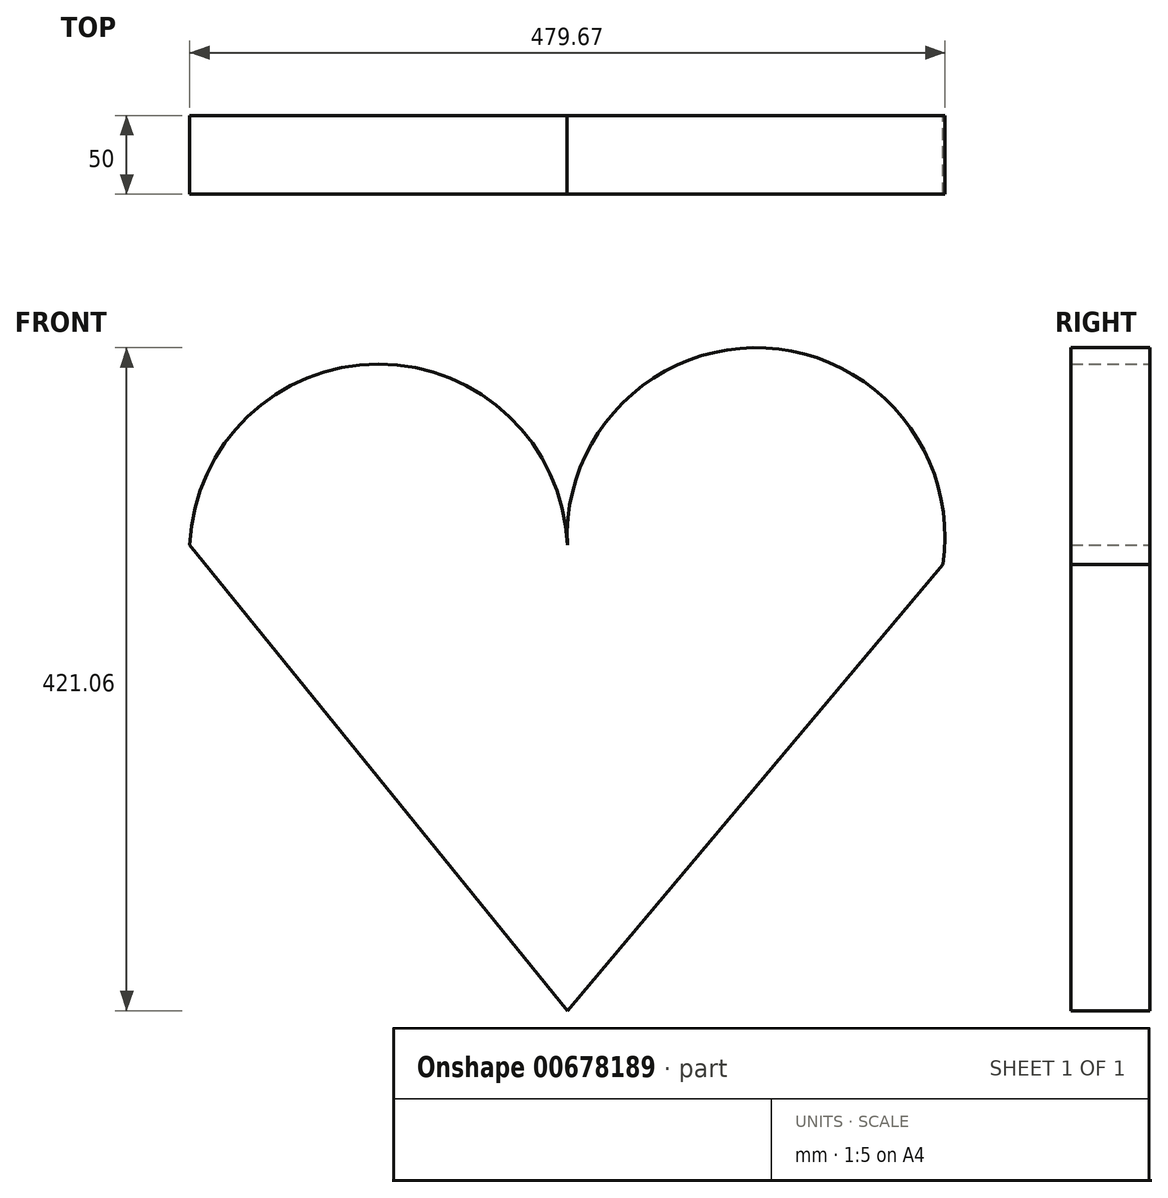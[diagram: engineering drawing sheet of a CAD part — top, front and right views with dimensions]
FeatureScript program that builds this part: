
annotation { "Feature Type Name" : "Feature", "Feature Type Description" : "" }
export const myFeature = defineFeature(function(context is Context, id is Id, definition is map)
    precondition{}
    {
        {
            var Q0;
            Q0=qCreatedBy(makeId("Front.planeOp"),FACE);
            var sketch = newSketch(context, id + "F0", { "sketchPlane" : qUnion([Q0])});
            skCircle(sketch, "E0", {"center": v(0, 0) * mm, "radius": 53.72 * mm});
            skCircle(sketch, "E1", {"center": v(0, 0) * mm, "radius": 58.65 * mm, "construction": true});
            skCircle(sketch, "E2", {"center": v(0, 0) * mm, "radius": 63.5 * mm, "construction": true});
            skLineSegment(sketch, "E3", {"start": v(0, 0) * mm, "end": v(0, 78.84) * mm, "construction": true});
            skLineSegment(sketch, "E4", {"start": v(0, 0) * mm, "end": v(-5.91, 90.2) * mm, "construction": true});
            skPoint(sketch, "E5.startSnap0", {"position": v(0, 39.42) * mm});
            skLineSegment(sketch, "E6", {"start": v(0, 58.65) * mm, "end": v(-64.13, 58.65) * mm, "construction": true});
            skLineSegment(sketch, "E7", {"start": v(0, 58.65) * mm, "end": v(-66.32, 34.51) * mm, "construction": true});
            skCircle(sketch, "E8", {"center": v(0, 0) * mm, "radius": 55.11 * mm, "construction": true});
            skCircle(sketch, "E9", {"center": v(0, 58.65) * mm, "radius": 14.6 * mm, "construction": true});
            skCircle(sketch, "E10", {"center": v(-13.72, 53.65) * mm, "radius": 14.6 * mm, "construction": true});
            skArc(sketch, "E11", {"start": v(0.88, 53.71) * mm, "mid": v(0.64, 56.22) * mm, "end": v(0, 58.65) * mm});
            skArc(sketch, "E12", {"start": v(0, 58.65) * mm, "mid": v(-1.1, 61.03) * mm, "end": v(-2.63, 63.15) * mm});
            skArc(sketch, "E13.MirrorCS", {"start": v(-7.66, 58.15) * mm, "mid": v(-6.88, 60.65) * mm, "end": v(-5.64, 62.95) * mm});
            skCircle(sketch, "E14.MirrorC", {"center": v(6.6, 54.99) * mm, "radius": 14.6 * mm, "construction": true});
            skArc(sketch, "E15.MirrorCS", {"start": v(-7.88, 53.14) * mm, "mid": v(-7.97, 55.65) * mm, "end": v(-7.66, 58.15) * mm});
            skArc(sketch, "E16", {"start": v(-2.63, 63.15) * mm, "mid": v(-4.14, 63.24) * mm, "end": v(-5.64, 62.95) * mm});
            skCircle(sketch, "E17", {"center": v(0, 0) * mm, "radius": 37.5 * mm});
            skLineSegment(sketch, "E18", {"start": v(-18.41, 23.71) * mm, "end": v(-5.46, 4.6) * mm});
            skLineSegment(sketch, "E19", {"start": v(-5.46, 4.6) * mm, "end": v(1.07, 20.93) * mm});
            skLineSegment(sketch, "E20", {"start": v(1.07, 20.93) * mm, "end": v(16.07, -7.38) * mm});
            skLineSegment(sketch, "E21", {"start": v(16.07, -7.38) * mm, "end": v(-13.09, -2.9) * mm});
            skLineSegment(sketch, "E22", {"start": v(-13.09, -2.9) * mm, "end": v(-18.41, 23.71) * mm});
            skSolve(sketch);
        }
        {
            var Q0;
            {var subQ0=sQuery(id+"F0.wireOp",EDGE,"E0");var subQ1=makeQuery(id+"F0.imprint","INTERSECT",VERTEX,{"derivedFrom":[subQ0,sQuery(id+"F0.wireOp",EDGE,"E11")]});Q0=makeQuery(id+"F0.imprint","IMPRINT",FACE,{"disambiguationData":[TD([[makeQuery(id+"F0.imprint","IMPRINT",EDGE,{"disambiguationData":[TD([[subQ1,-1.0]])],"derivedFrom":subQ0}),1.0]])]});}
            var Q1;
            {var subQ0=sQuery(id+"F0.wireOp",EDGE,"E11");Q1=makeQuery(id+"F0.imprint","IMPRINT",FACE,{"disambiguationData":[TD([[makeQuery(id+"F0.imprint","IMPRINT",EDGE,{"derivedFrom":subQ0}),1.0]])]});}
            extrude(context, id + "F1", {"entities" : qUnion([Q0, Q1]), "depth" : 25 * mm, "offsetDistance" : 25 * mm});
        }
        {
            var Q0;
            Q0=makeQuery(id+"F1.opExtrude","SWEPT_BODY",BODY,{"disambiguationData":[OSD([sQuery(id+"F0.wireOp",EDGE,"E0"),sQuery(id+"F0.wireOp",EDGE,"E11"),sQuery(id+"F0.wireOp",EDGE,"E12"),sQuery(id+"F0.wireOp",EDGE,"E13.MirrorCS"),sQuery(id+"F0.wireOp",EDGE,"E15.MirrorCS"),sQuery(id+"F0.wireOp",EDGE,"E16")])]});
            var Q1;
            Q1=makeQuery(id+"F1.opExtrude","SWEPT_FACE",FACE,{"disambiguationData":[OSD([sQuery(id+"F0.wireOp",EDGE,"E0")])]});
            circularPattern(context, id + "F2", {"entities" : qUnion([Q0]), "axis" : qUnion([Q1]), "angle" : 360 * degree, "instanceCount" : 24, "equalSpace" : true});
        }
        {
            var Q0;
            Q0=makeQuery(id+"F0.imprint","IMPRINT",FACE,{"disambiguationData":[TD([[makeQuery(id+"F0.imprint","IMPRINT",EDGE,{"derivedFrom":sQuery(id+"F0.wireOp",EDGE,"E17")}),1.0]])]});
            extrude(context, id + "F3", {"entities" : qUnion([Q0]), "operationType" : NewBodyOperationType.ADD, "depth" : 35 * mm, "offsetDistance" : 25 * mm});
        }
        {
            var Q0;
            {var subQ0=sQuery(id+"F0.wireOp",EDGE,"E17");var subQ1=makeQuery(id+"F1.opExtrude","CAP_FACE",FACE,{"disambiguationData":[OSD([sQuery(id+"F0.wireOp",EDGE,"E0"),sQuery(id+"F0.wireOp",EDGE,"E11"),sQuery(id+"F0.wireOp",EDGE,"E12"),sQuery(id+"F0.wireOp",EDGE,"E13.MirrorCS"),sQuery(id+"F0.wireOp",EDGE,"E15.MirrorCS"),sQuery(id+"F0.wireOp",EDGE,"E16"),subQ0])],"isStart":true});Q0=makeQuery(id+"F3.boolean.opBoolean","MERGE",FACE,{"derivedFrom":[subQ1,makeQuery(id+"F2.opPattern","COPY",FACE,{"derivedFrom":subQ1,"instanceName":"1"}),makeQuery(id+"F2.opPattern","COPY",FACE,{"derivedFrom":subQ1,"instanceName":"2"}),makeQuery(id+"F2.opPattern","COPY",FACE,{"derivedFrom":subQ1,"instanceName":"3"}),makeQuery(id+"F2.opPattern","COPY",FACE,{"derivedFrom":subQ1,"instanceName":"4"}),makeQuery(id+"F2.opPattern","COPY",FACE,{"derivedFrom":subQ1,"instanceName":"5"}),makeQuery(id+"F2.opPattern","COPY",FACE,{"derivedFrom":subQ1,"instanceName":"6"}),makeQuery(id+"F2.opPattern","COPY",FACE,{"derivedFrom":subQ1,"instanceName":"7"}),makeQuery(id+"F2.opPattern","COPY",FACE,{"derivedFrom":subQ1,"instanceName":"8"}),makeQuery(id+"F2.opPattern","COPY",FACE,{"derivedFrom":subQ1,"instanceName":"9"}),makeQuery(id+"F2.opPattern","COPY",FACE,{"derivedFrom":subQ1,"instanceName":"10"}),makeQuery(id+"F2.opPattern","COPY",FACE,{"derivedFrom":subQ1,"instanceName":"11"}),makeQuery(id+"F2.opPattern","COPY",FACE,{"derivedFrom":subQ1,"instanceName":"12"}),makeQuery(id+"F2.opPattern","COPY",FACE,{"derivedFrom":subQ1,"instanceName":"13"}),makeQuery(id+"F2.opPattern","COPY",FACE,{"derivedFrom":subQ1,"instanceName":"14"}),makeQuery(id+"F2.opPattern","COPY",FACE,{"derivedFrom":subQ1,"instanceName":"15"}),makeQuery(id+"F2.opPattern","COPY",FACE,{"derivedFrom":subQ1,"instanceName":"16"}),makeQuery(id+"F2.opPattern","COPY",FACE,{"derivedFrom":subQ1,"instanceName":"17"}),makeQuery(id+"F2.opPattern","COPY",FACE,{"derivedFrom":subQ1,"instanceName":"18"}),makeQuery(id+"F2.opPattern","COPY",FACE,{"derivedFrom":subQ1,"instanceName":"19"}),makeQuery(id+"F2.opPattern","COPY",FACE,{"derivedFrom":subQ1,"instanceName":"20"}),makeQuery(id+"F2.opPattern","COPY",FACE,{"derivedFrom":subQ1,"instanceName":"21"}),makeQuery(id+"F2.opPattern","COPY",FACE,{"derivedFrom":subQ1,"instanceName":"22"}),makeQuery(id+"F2.opPattern","COPY",FACE,{"derivedFrom":subQ1,"instanceName":"23"}),makeQuery(id+"F3.opExtrude","CAP_FACE",FACE,{"disambiguationData":[OSD([subQ0,sQuery(id+"F0.wireOp",EDGE,"E18"),sQuery(id+"F0.wireOp",EDGE,"E19"),sQuery(id+"F0.wireOp",EDGE,"E20"),sQuery(id+"F0.wireOp",EDGE,"E21"),sQuery(id+"F0.wireOp",EDGE,"E22")])],"isStart":true})]});}
            chamfer(context, id + "F4", {"entities" : qUnion([Q0]), "width" : 1 * mm, "tangentPropagation" : true});
        }
        {
            var Q0;
            Q0=qCreatedBy(makeId("Front.planeOp"),FACE);
            var sketch = newSketch(context, id + "F5", { "sketchPlane" : qUnion([Q0])});
            skArc(sketch, "E23", {"start": v(238.57, 66.06) * mm, "mid": v(126.17, 203.6) * mm, "end": v(0, 78.56) * mm});
            skArc(sketch, "E24", {"start": v(0, 78.56) * mm, "mid": v(-119.89, 193.4) * mm, "end": v(-239.78, 78.56) * mm});
            skLineSegment(sketch, "E25", {"start": v(0, -217.3) * mm, "end": v(-239.78, 78.56) * mm});
            skLineSegment(sketch, "E26", {"start": v(0, -217.3) * mm, "end": v(238.57, 66.06) * mm});
            skSolve(sketch);
        }
        {
            var Q0;
            {var subQ0=sQuery(id+"F5.wireOp",EDGE,"E23");Q0=makeQuery(id+"F5.imprint","IMPRINT",FACE,{"disambiguationData":[TD([[makeQuery(id+"F5.imprint","IMPRINT",EDGE,{"derivedFrom":subQ0}),1.0]])]});}
            extrude(context, id + "F6", {"entities" : qUnion([Q0]), "operationType" : NewBodyOperationType.ADD, "depth" : 50 * mm, "offsetDistance" : 25 * mm});
        }
    });
